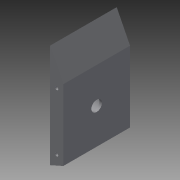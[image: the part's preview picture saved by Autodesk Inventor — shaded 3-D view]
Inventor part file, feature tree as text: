
AUTODESK INVENTOR PART (.ipt)
format: ipt  version: 2015 (Build 190159000, 159)  size: 99,328 bytes
history: native  units: mm
features: extrude x3, sketch x2
ambient origin geometry x8: Origin, YZ Plane, XZ Plane, XY Plane, X Axis, Y Axis, Z Axis, Center Point
bodies: Solid1 (feature_tree)
feature tree (5):
  extrude  "Extrusion1"  Depth=10.0mm
  sketch  "Sketch2"  dims[d2=4.444444mm d3=77.444444mm d8=2.5mm d9=2.5mm d10=50.0mm d11=0.0mm d12=25.0mm d13=15.0mm d14=10.0mm d15=0.0mm d16=8.0mm d17=2.0mm d18=0.0mm]
  extrude  "Extrusion2"  Depth=2.0mm
  extrude  "Extrusion3"  Depth=2.0mm
  sketch  "Sketch1"  dims[d0=10.0mm d1=53.0mm]
